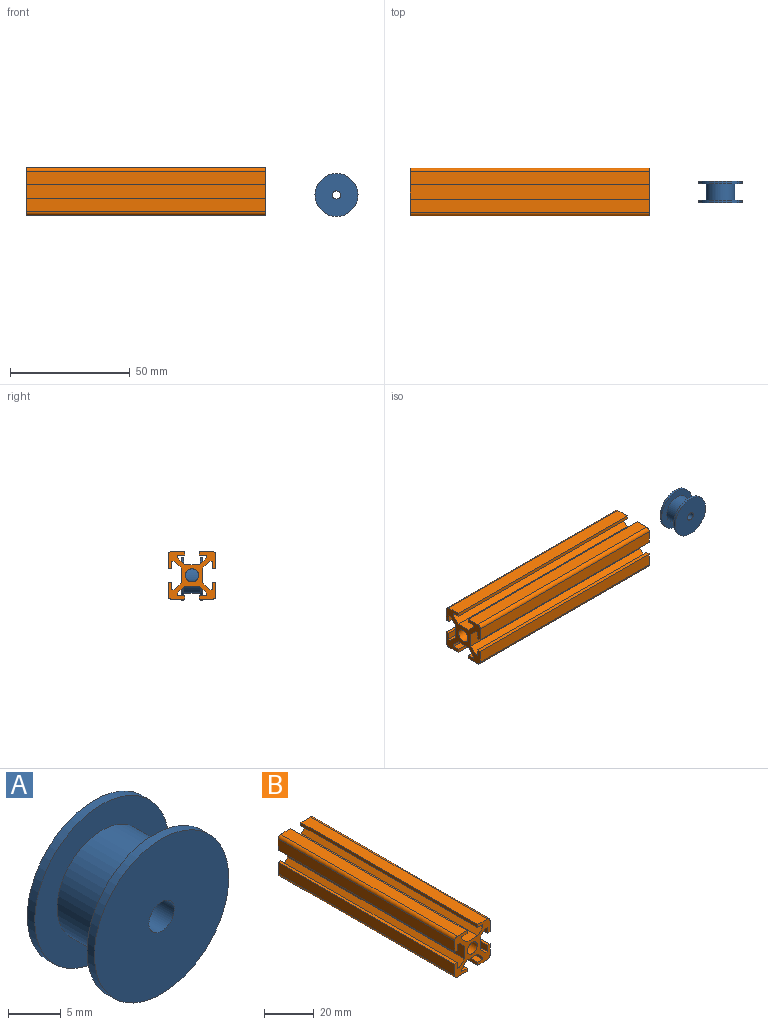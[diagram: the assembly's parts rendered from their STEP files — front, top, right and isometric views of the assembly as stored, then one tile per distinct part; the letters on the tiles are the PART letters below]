
ASSEMBLY  parts=2 mates=1
PART A: 8 faces, bbox 18x9x18 mm
  f0: plane 18x18mm, normal (0,1,0), area 245.4mm2, adj f6,f7
  f1: plane 18x18mm, normal (0,-1,0), area 245.4mm2, adj f2,f7
  f2: cylinder r=9mm len=18mm, axis (0,1,0), area 56.5mm2, adj f1,f3
  f3: plane 18x18mm, normal (0,1,0), area 141.4mm2, adj f2,f4
  f4: cylinder r=6mm len=12mm, axis (0,1,0), area 263.9mm2, adj f3,f5
  f5: plane 18x18mm, normal (0,-1,0), area 141.4mm2, adj f4,f6
  f6: cylinder r=9mm len=18mm, axis (0,1,0), area 56.5mm2, adj f0,f5
  f7: cylinder r=1.7mm len=9mm, axis (0,-1,0), area 96.1mm2, adj f0,f1
PART B: 51 faces, bbox 20x100x20 mm
  f0: plane 100x3mm, normal (0,0,1), area 300mm2, adj f35,f37,f38,f50
  f1: plane 100x3mm, normal (0,0,1), area 300mm2, adj f11,f37,f38,f49
  f2: plane 100x3mm, normal (1,0,0), area 300mm2, adj f32,f37,f38,f48
  f3: plane 100x3mm, normal (1,0,0), area 300mm2, adj f28,f37,f38,f47
  f4: plane 100x3mm, normal (-1,0,0), area 300mm2, adj f18,f37,f38,f46
  f5: plane 100x3mm, normal (-1,0,0), area 300mm2, adj f14,f37,f38,f45
  f6: plane 100x3mm, normal (0,0,-1), area 300mm2, adj f21,f37,f38,f44
  f7: plane 100x3mm, normal (0,0,-1), area 300mm2, adj f25,f37,f38,f43
  f8: plane 100x2.91mm, normal (0.71,0,-0.71), area 412.1mm2, adj f9,f37,f38,f50
  f9: plane 100x6.17mm, normal (0,0,-1), area 617.2mm2, adj f8,f10,f37,f38
  f10: plane 100x2.91mm, normal (-0.71,0,-0.71), area 412.1mm2, adj f9,f37,f38,f49
  f11: plane 100x1.5mm, normal (-1,0,0), area 150mm2, adj f1,f12,f37,f38
  f12: plane 100x5.5mm, normal (0,0,-1), area 550mm2, adj f11,f37,f38,f42
  f13: plane 100x5.5mm, normal (1,0,0), area 550mm2, adj f14,f37,f38,f42
  f14: plane 100x1.5mm, normal (0,0,1), area 150mm2, adj f5,f13,f37,f38
  f15: plane 100x2.91mm, normal (0.71,0,0.71), area 412.1mm2, adj f16,f37,f38,f45
  f16: plane 100x6.17mm, normal (1,0,0), area 617.2mm2, adj f15,f17,f37,f38
  f17: plane 100x2.91mm, normal (0.71,0,-0.71), area 412.1mm2, adj f16,f37,f38,f46
  f18: plane 100x1.5mm, normal (0,0,-1), area 150mm2, adj f4,f19,f37,f38
  f19: plane 100x5.5mm, normal (1,0,0), area 550mm2, adj f18,f37,f38,f41
  f20: plane 100x5.5mm, normal (0,0,1), area 550mm2, adj f21,f37,f38,f41
  f21: plane 100x1.5mm, normal (-1,0,0), area 150mm2, adj f6,f20,f37,f38
  f22: plane 100x2.91mm, normal (-0.71,0,0.71), area 412.1mm2, adj f23,f37,f38,f44
  f23: plane 100x6.17mm, normal (0,0,1), area 617.2mm2, adj f22,f24,f37,f38
  f24: plane 100x2.91mm, normal (0.71,0,0.71), area 412.1mm2, adj f23,f37,f38,f43
  f25: plane 100x1.5mm, normal (1,0,0), area 150mm2, adj f7,f26,f37,f38
  f26: plane 100x5.5mm, normal (0,0,1), area 550mm2, adj f25,f37,f38,f40
  f27: plane 100x5.5mm, normal (-1,0,0), area 550mm2, adj f28,f37,f38,f40
  f28: plane 100x1.5mm, normal (0,0,-1), area 150mm2, adj f3,f27,f37,f38
  f29: plane 100x2.91mm, normal (-0.71,0,-0.71), area 412.1mm2, adj f30,f37,f38,f47
  f30: plane 100x6.17mm, normal (-1,0,0), area 617.2mm2, adj f29,f31,f37,f38
  f31: plane 100x2.91mm, normal (-0.71,0,0.71), area 412.1mm2, adj f30,f37,f38,f48
  f32: plane 100x1.5mm, normal (0,0,1), area 150mm2, adj f2,f33,f37,f38
  f33: plane 100x5.5mm, normal (-1,0,0), area 550mm2, adj f32,f37,f38,f39
  f34: plane 100x5.5mm, normal (0,0,-1), area 550mm2, adj f35,f37,f38,f39
  f35: plane 100x1.5mm, normal (1,0,0), area 150mm2, adj f0,f34,f37,f38
  f36: cylinder r=2.75mm len=100mm, axis (0,1,0), area 1727.9mm2, adj f37,f38
  f37: plane 20x20mm, normal (0,-1,0), area 180.3mm2, adj f0,f1,f2,f3,f4,f5,f6,f7
  f38: plane 20x20mm, normal (0,1,0), area 180.3mm2, adj f0,f1,f2,f3,f4,f5,f6,f7
  f39: cylinder r=1.5mm len=100mm, axis (0,1,0), area 235.6mm2, adj f33,f34,f37,f38
  f40: cylinder r=1.5mm len=100mm, axis (0,-1,0), area 235.6mm2, adj f26,f27,f37,f38
  f41: cylinder r=1.5mm len=100mm, axis (0,1,0), area 235.6mm2, adj f19,f20,f37,f38
  f42: cylinder r=1.5mm len=100mm, axis (0,-1,0), area 235.6mm2, adj f12,f13,f37,f38
  f43: plane 100x1.09mm, normal (1,0,0), area 108.6mm2, adj f7,f24,f37,f38
  f44: plane 100x1.09mm, normal (-1,0,0), area 108.6mm2, adj f6,f22,f37,f38
  f45: plane 100x1.09mm, normal (0,0,1), area 108.6mm2, adj f5,f15,f37,f38
  f46: plane 100x1.09mm, normal (0,0,-1), area 108.6mm2, adj f4,f17,f37,f38
  f47: plane 100x1.09mm, normal (0,0,-1), area 108.6mm2, adj f3,f29,f37,f38
  f48: plane 100x1.09mm, normal (0,0,1), area 108.6mm2, adj f2,f31,f37,f38
  f49: plane 100x1.09mm, normal (-1,0,0), area 108.6mm2, adj f1,f10,f37,f38
  f50: plane 100x1.09mm, normal (1,0,0), area 108.6mm2, adj f0,f8,f37,f38
PLACE A rot(axis=(0,1,0),180deg) t=(55.78,-20.14,15.08)mm
PLACE B rot(axis=(0,0,-1),90deg) t=(-24.12,-20.14,16.58)mm
MATE parallel A.f2 <-> B.f19  axis (0,-1,0) through (55.78,-24.64,15.08)mm
